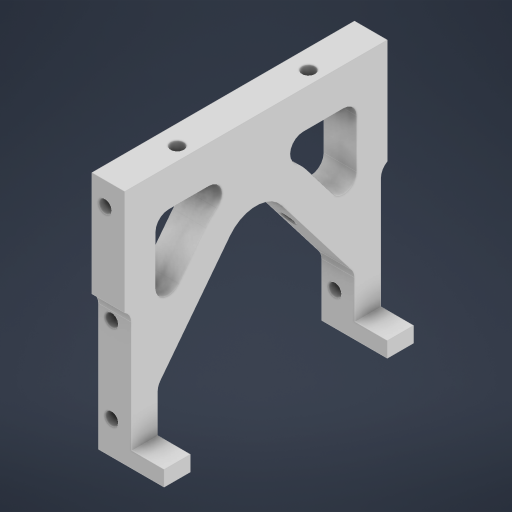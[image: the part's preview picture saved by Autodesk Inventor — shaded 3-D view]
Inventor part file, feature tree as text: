
AUTODESK INVENTOR PART (.ipt)
format: ipt  version: 2024 (Build 280153000, 153)  size: 335,360 bytes
history: native  units: mm
features: extrude x6, sketch x6, fillet x3, other x1, projected_geometry x1
ambient origin geometry x8: Origin, YZ Plane, XZ Plane, XY Plane, X Axis, Y Axis, Z Axis, Center Point
bodies: Body1 (feature_tree)
feature tree (17):
  other  "Твердое тело1"
  extrude  "Выдавливание1"  Depth=80.0mm
  fillet  "Сопряжение1"  Radius=2.0mm
  fillet  "Сопряжение3"  Radius=2.0mm
  sketch  "Эскиз2"
  sketch  "Эскиз3"
  extrude  "Выдавливание2"  Depth=2.0mm
  extrude  "Выдавливание3"  Depth=2.0mm
  extrude  "Выдавливание4"  Depth=44.0mm
  extrude  "Выдавливание5"  Depth=44.0mm
  fillet  "Сопряжение4"  Radius=40.0mm
  extrude  "Выдавливание6"  Depth=40.0mm
  sketch  "Эскиз1"
  sketch  "Эскиз4"
  projected_geometry  "Спроецированная петля1"
  sketch  "Эскиз5"
  sketch  "Эскиз6"
